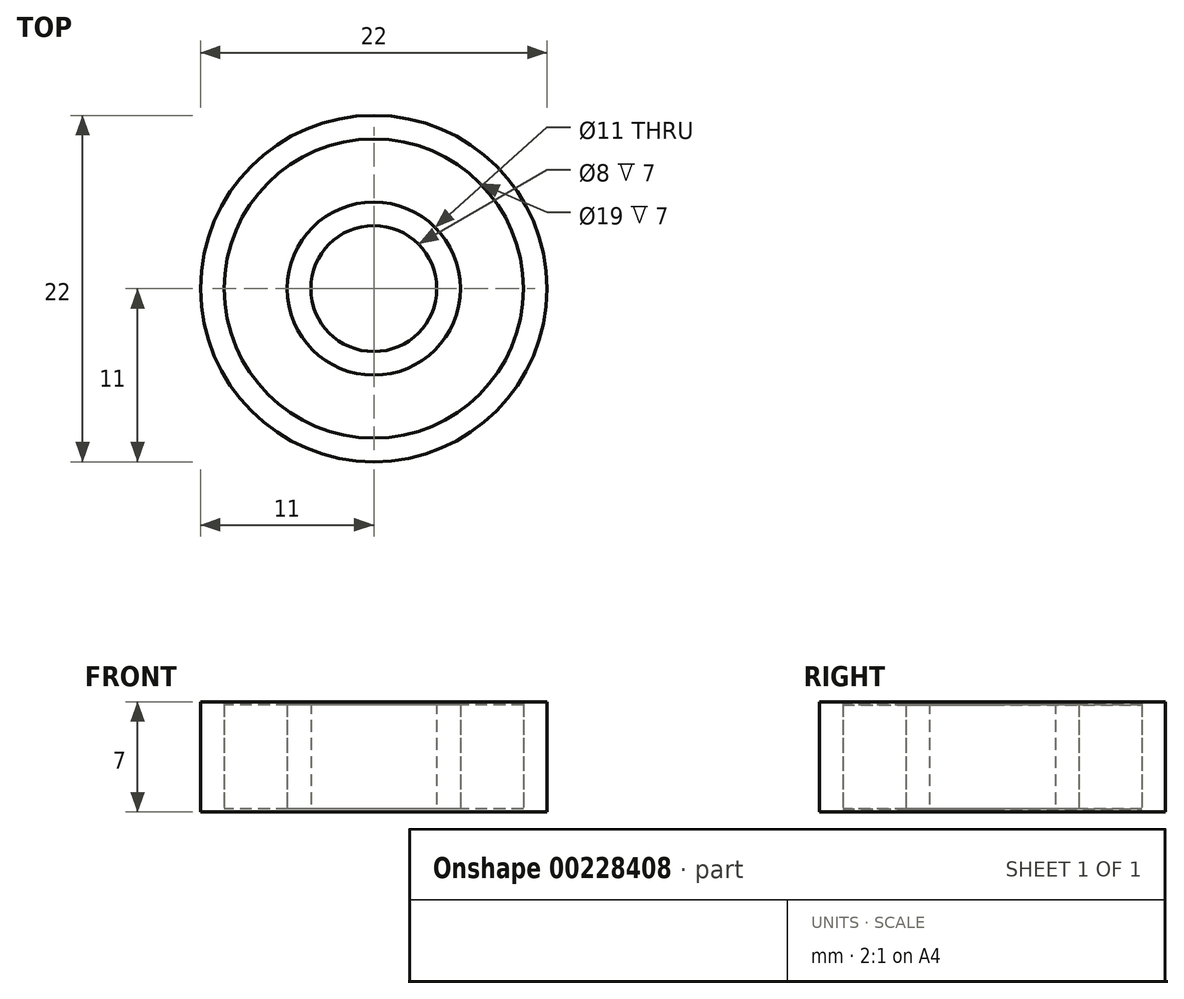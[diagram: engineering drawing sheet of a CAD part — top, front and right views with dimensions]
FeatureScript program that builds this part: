
annotation { "Feature Type Name" : "Feature", "Feature Type Description" : "" }
export const myFeature = defineFeature(function(context is Context, id is Id, definition is map)
    precondition{}
    {
        {
            assignVariable(context, id + "F0", {"name" : "index", "anyValue" : 1});
        }
        {
            assignVariable(context, id + "F1", {"name" : "width", "anyValue" : [6, 7, 7, 5, 5, 6, 7][getVariable(context, 'index')]});
        }
        {
            var Q0;
            Q0=qCreatedBy(makeId("Top.planeOp"),FACE);
            var sketch = newSketch(context, id + "F2", { "sketchPlane" : qUnion([Q0])});
            skCircle(sketch, "E0", {"center": v(0, 0) * mm, "radius": 4 * mm});
            skCircle(sketch, "E1", {"center": v(0, 0) * mm, "radius": 5.5 * mm});
            skCircle(sketch, "E2", {"center": v(0, 0) * mm, "radius": 11 * mm});
            skCircle(sketch, "E3", {"center": v(0, 0) * mm, "radius": 9.5 * mm});
            skSolve(sketch);
        }
        {
            var Q0;
            Q0 = qSketchRegion(id + "F2", true);
            var Q1;
            Q1=makeQuery(id+"F2.imprint","IMPRINT",FACE,{"disambiguationData":[TD([[makeQuery(id+"F2.imprint","IMPRINT",EDGE,{"derivedFrom":sQuery(id+"F2.wireOp",EDGE,"E0")}),-1.0]])]});
            extrude(context, id + "F3", {"entities" : qUnion([Q0, Q1]), "endBound" : BoundingType.SYMMETRIC, "depth" : (getVariable(context, 'width')) * mm});
        }
        {
            var Q0;
            Q0=makeQuery(id+"F2.imprint","IMPRINT",FACE,{"disambiguationData":[TD([[makeQuery(id+"F2.imprint","IMPRINT",EDGE,{"derivedFrom":sQuery(id+"F2.wireOp",EDGE,"E1")}),-1.0]])]});
            extrude(context, id + "F4", {"entities" : qUnion([Q0]), "endBound" : BoundingType.SYMMETRIC, "depth" : (getVariable(context, 'width') - 0.4) * mm});
        }
    });
